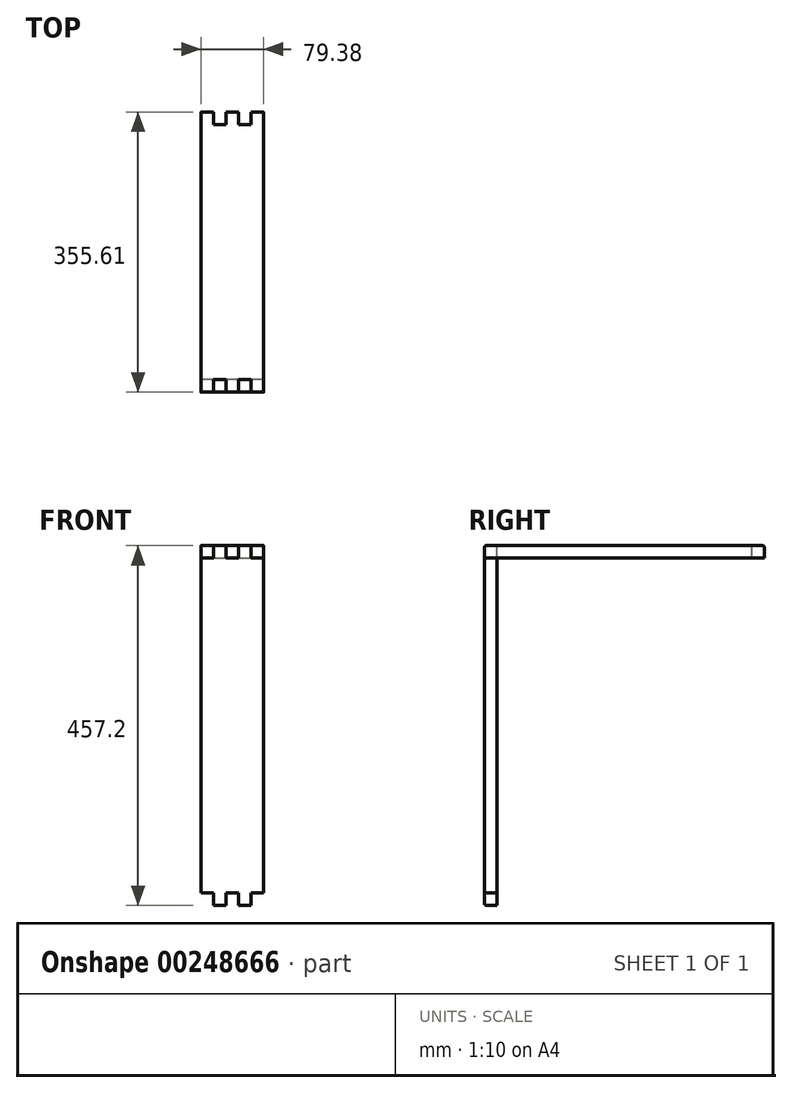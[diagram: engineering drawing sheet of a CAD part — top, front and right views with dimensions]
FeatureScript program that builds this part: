
annotation { "Feature Type Name" : "Feature", "Feature Type Description" : "" }
export const myFeature = defineFeature(function(context is Context, id is Id, definition is map)
    precondition{}
    {
        {
            var Q0;
            Q0=qCreatedBy(makeId("Front.planeOp"),FACE);
            var sketch = newSketch(context, id + "F0", { "sketchPlane" : qUnion([Q0])});
            skLineSegment(sketch, "E0.bottom", {"start": v(0, 0) * mm, "end": v(79.38, 0) * mm});
            skLineSegment(sketch, "E0.top", {"start": v(0, 457.2) * mm, "end": v(79.37, 457.2) * mm});
            skLineSegment(sketch, "E0.left", {"start": v(0, 0) * mm, "end": v(0, 457.2) * mm});
            skLineSegment(sketch, "E0.right", {"start": v(79.38, 0) * mm, "end": v(79.37, 457.2) * mm});
            skSolve(sketch);
        }
        {
            var Q0;
            Q0 = qSketchRegion(id + "F0", true);
            extrude(context, id + "F1", {"entities" : qUnion([Q0]), "depth" : 15.88 * mm});
        }
        {
            var Q0;
            Q0=makeQuery(id+"F1.opExtrude","CAP_FACE",FACE,{"disambiguationData":[OSD([sQuery(id+"F0.wireOp",EDGE,"E0.bottom"),sQuery(id+"F0.wireOp",EDGE,"E0.top"),sQuery(id+"F0.wireOp",EDGE,"E0.left"),sQuery(id+"F0.wireOp",EDGE,"E0.right")])],"isStart":false});
            var sketch = newSketch(context, id + "F2", { "sketchPlane" : qUnion([Q0])});
            skLineSegment(sketch, "E1.bottom", {"start": v(0, 457.2) * mm, "end": v(15.87, 457.2) * mm});
            skLineSegment(sketch, "E1.top", {"start": v(0, 441.33) * mm, "end": v(15.88, 441.33) * mm});
            skLineSegment(sketch, "E1.left", {"start": v(0, 457.2) * mm, "end": v(0, 441.33) * mm});
            skLineSegment(sketch, "E1.right", {"start": v(15.88, 457.2) * mm, "end": v(15.88, 441.33) * mm});
            skLineSegment(sketch, "E2.0.1.0", {"start": v(0, 15.88) * mm, "end": v(15.87, 15.88) * mm});
            skLineSegment(sketch, "E2.0.1.1", {"start": v(15.88, 15.88) * mm, "end": v(15.88, 0) * mm});
            skLineSegment(sketch, "E2.0.1.2", {"start": v(0, 0) * mm, "end": v(15.88, 0) * mm});
            skLineSegment(sketch, "E2.0.1.3", {"start": v(0, 15.88) * mm, "end": v(0, 0) * mm});
            skLineSegment(sketch, "E2.1.0.0", {"start": v(31.75, 457.2) * mm, "end": v(47.62, 457.2) * mm});
            skLineSegment(sketch, "E2.1.0.1", {"start": v(47.62, 457.2) * mm, "end": v(47.62, 441.33) * mm});
            skLineSegment(sketch, "E2.1.0.2", {"start": v(31.75, 441.33) * mm, "end": v(47.62, 441.33) * mm});
            skLineSegment(sketch, "E2.1.0.3", {"start": v(31.75, 457.2) * mm, "end": v(31.75, 441.33) * mm});
            skLineSegment(sketch, "E2.1.1.0", {"start": v(31.75, 15.88) * mm, "end": v(47.62, 15.88) * mm});
            skLineSegment(sketch, "E2.1.1.1", {"start": v(47.62, 15.88) * mm, "end": v(47.62, 0) * mm});
            skLineSegment(sketch, "E2.1.1.2", {"start": v(31.75, 0) * mm, "end": v(47.62, 0) * mm});
            skLineSegment(sketch, "E2.1.1.3", {"start": v(31.75, 15.88) * mm, "end": v(31.75, 0) * mm});
            skLineSegment(sketch, "E2.2.0.0", {"start": v(63.5, 457.2) * mm, "end": v(79.38, 457.2) * mm});
            skLineSegment(sketch, "E2.2.0.1", {"start": v(79.38, 457.2) * mm, "end": v(79.38, 441.33) * mm});
            skLineSegment(sketch, "E2.2.0.2", {"start": v(63.5, 441.33) * mm, "end": v(79.38, 441.33) * mm});
            skLineSegment(sketch, "E2.2.0.3", {"start": v(63.5, 457.2) * mm, "end": v(63.5, 441.33) * mm});
            skLineSegment(sketch, "E2.2.1.0", {"start": v(63.5, 15.88) * mm, "end": v(79.38, 15.88) * mm});
            skLineSegment(sketch, "E2.2.1.1", {"start": v(79.38, 15.88) * mm, "end": v(79.38, 0) * mm});
            skLineSegment(sketch, "E2.2.1.2", {"start": v(63.5, 0) * mm, "end": v(79.38, 0) * mm});
            skLineSegment(sketch, "E2.2.1.3", {"start": v(63.5, 15.88) * mm, "end": v(63.5, 0) * mm});
            skLineSegment(sketch, "E2.direction1", {"start": v(0, 457.2) * mm, "end": v(31.75, 457.2) * mm, "construction": true});
            skLineSegment(sketch, "E2.direction2", {"start": v(0, 457.2) * mm, "end": v(0, 15.88) * mm, "construction": true});
            skSolve(sketch);
        }
        {
            var Q0;
            Q0 = qSketchRegion(id + "F2", true);
            extrude(context, id + "F3", {"entities" : qUnion([Q0]), "operationType" : NewBodyOperationType.REMOVE, "endBound" : BoundingType.UP_TO_NEXT, "oppositeDirection" : true, "depth" : 25.4 * mm});
        }
        {
            var Q0;
            {var subQ2=sQuery(id+"F0.wireOp",EDGE,"E0.top");Q0=makeQuery(id+"F3.boolean.opBoolean","SPLIT",FACE,{"disambiguationData":[TD([makeQuery(id+"F3.opExtrude","SWEPT_FACE",FACE,{"disambiguationData":[OSD([sQuery(id+"F2.wireOp",EDGE,"E1.right")])]})])],"derivedFrom":makeQuery(id+"F1.opExtrude","SWEPT_FACE",FACE,{"disambiguationData":[OSD([subQ2])]})});}
            var sketch = newSketch(context, id + "F4", { "sketchPlane" : qUnion([Q0])});
            skLineSegment(sketch, "E3.0", {"start": v(0, 0) * mm, "end": v(0, -15.87) * mm, "construction": true});
            skLineSegment(sketch, "E3.1", {"start": v(0, -15.88) * mm, "end": v(15.88, -15.88) * mm, "construction": true});
            skLineSegment(sketch, "E4.bottom", {"start": v(0, -15.87) * mm, "end": v(79.37, -15.87) * mm});
            skLineSegment(sketch, "E4.top", {"start": v(0, 339.73) * mm, "end": v(79.37, 339.73) * mm});
            skLineSegment(sketch, "E4.left", {"start": v(0, -15.87) * mm, "end": v(0, 339.73) * mm});
            skLineSegment(sketch, "E4.right", {"start": v(79.37, -15.88) * mm, "end": v(79.37, 339.73) * mm});
            skLineSegment(sketch, "E5.0", {"start": v(79.37, 0) * mm, "end": v(79.37, -15.87) * mm, "construction": true});
            skSolve(sketch);
        }
        {
            var Q0;
            Q0 = qSketchRegion(id + "F4", true);
            extrude(context, id + "F5", {"entities" : qUnion([Q0]), "oppositeDirection" : true, "depth" : 15.88 * mm});
        }
        {
            var Q0;
            Q0=makeQuery(id+"F1.opExtrude","SWEPT_BODY",BODY,{"disambiguationData":[OSD([sQuery(id+"F0.wireOp",EDGE,"E0.bottom"),sQuery(id+"F0.wireOp",EDGE,"E0.top"),sQuery(id+"F0.wireOp",EDGE,"E0.left"),sQuery(id+"F0.wireOp",EDGE,"E0.right")])]});
            var Q1;
            Q1=makeQuery(id+"F5.opExtrude","SWEPT_BODY",BODY,{"disambiguationData":[OSD([sQuery(id+"F4.wireOp",EDGE,"E4.bottom"),sQuery(id+"F4.wireOp",EDGE,"E4.top"),sQuery(id+"F4.wireOp",EDGE,"E4.left"),sQuery(id+"F4.wireOp",EDGE,"E4.right")])]});
            booleanBodies(context, id + "F6", {"operationType" : BooleanOperationType.SUBTRACTION, "tools" : qUnion([Q0]), "targets" : qUnion([Q1]), "keepTools" : true});
        }
        {
            var Q0;
            {var subQ3=sQuery(id+"F4.wireOp",EDGE,"E4.bottom");Q0=makeQuery(id+"F6.opBoolean","SPLIT",FACE,{"disambiguationData":[TD([makeQuery(id+"F3.boolean.opBoolean","COPY",FACE,{"derivedFrom":makeQuery(id+"F3.opExtrude","SWEPT_FACE",FACE,{"disambiguationData":[OSD([sQuery(id+"F2.wireOp",EDGE,"E1.right")])]})})])],"derivedFrom":makeQuery(id+"F5.opExtrude","SWEPT_FACE",FACE,{"disambiguationData":[OSD([subQ3])]})});}
            var Q1;
            Q1=makeQuery(id+"F5.opExtrude","SWEPT_FACE",FACE,{"disambiguationData":[OSD([sQuery(id+"F4.wireOp",EDGE,"E4.top")])]});
            cPlane(context, id + "F7", {"entities" : qUnion([Q0, Q1]), "cplaneType" : CPlaneType.MID_PLANE, "offset" : 25.4 * mm, "width" : 152.4 * mm, "height" : 152.4 * mm});
        }
        {
            var Q0;
            Q0=makeQuery(id+"F5.opExtrude","CAP_FACE",FACE,{"disambiguationData":[OSD([sQuery(id+"F4.wireOp",EDGE,"E4.bottom"),sQuery(id+"F4.wireOp",EDGE,"E4.top"),sQuery(id+"F4.wireOp",EDGE,"E4.left"),sQuery(id+"F4.wireOp",EDGE,"E4.right")])],"isStart":true});
            var sketch = newSketch(context, id + "F8", { "sketchPlane" : qUnion([Q0])});
            skLineSegment(sketch, "E6.0.0", {"start": v(31.75, 0) * mm, "end": v(15.88, 0) * mm, "construction": true});
            skLineSegment(sketch, "E6.0.1", {"start": v(15.88, 0) * mm, "end": v(15.88, -15.87) * mm, "construction": true});
            skLineSegment(sketch, "E6.0.2", {"start": v(15.88, -15.88) * mm, "end": v(31.75, -15.88) * mm, "construction": true});
            skLineSegment(sketch, "E6.0.3", {"start": v(31.75, -15.87) * mm, "end": v(31.75, 0) * mm, "construction": true});
            skLineSegment(sketch, "E6.1.0", {"start": v(63.5, -15.87) * mm, "end": v(63.5, 0) * mm, "construction": true});
            skLineSegment(sketch, "E6.1.1", {"start": v(63.5, 0) * mm, "end": v(47.62, 0) * mm, "construction": true});
            skLineSegment(sketch, "E6.1.2", {"start": v(47.62, 0) * mm, "end": v(47.62, -15.87) * mm, "construction": true});
            skLineSegment(sketch, "E6.1.3", {"start": v(47.62, -15.88) * mm, "end": v(63.5, -15.88) * mm, "construction": true});
            skLineSegment(sketch, "E7.MirrorCS", {"start": v(31.75, 339.72) * mm, "end": v(31.75, 323.85) * mm});
            skLineSegment(sketch, "E8.MirrorCS", {"start": v(63.5, 339.72) * mm, "end": v(63.5, 323.85) * mm});
            skLineSegment(sketch, "E9.MirrorCS", {"start": v(63.5, 323.85) * mm, "end": v(47.62, 323.85) * mm});
            skLineSegment(sketch, "E10.MirrorCS", {"start": v(47.62, 323.85) * mm, "end": v(47.62, 339.72) * mm});
            skLineSegment(sketch, "E11.MirrorCS", {"start": v(47.62, 339.73) * mm, "end": v(63.5, 339.73) * mm});
            skLineSegment(sketch, "E12.MirrorCS", {"start": v(15.88, 339.73) * mm, "end": v(31.75, 339.73) * mm});
            skLineSegment(sketch, "E13.MirrorCS", {"start": v(15.88, 323.85) * mm, "end": v(15.88, 339.72) * mm});
            skLineSegment(sketch, "E14.MirrorCS", {"start": v(31.75, 323.85) * mm, "end": v(15.88, 323.85) * mm});
            skSolve(sketch);
        }
        {
            var Q0;
            Q0=makeQuery(id+"F8.imprint","IMPRINT",FACE,{"disambiguationData":[TD([[makeQuery(id+"F8.imprint","IMPRINT",EDGE,{"derivedFrom":sQuery(id+"F8.wireOp",EDGE,"E7.MirrorCS")}),-1.0]])]});
            var Q1;
            Q1=makeQuery(id+"F8.imprint","IMPRINT",FACE,{"disambiguationData":[TD([[makeQuery(id+"F8.imprint","IMPRINT",EDGE,{"derivedFrom":sQuery(id+"F8.wireOp",EDGE,"E8.MirrorCS")}),-1.0]])]});
            var Q2;
            Q2 = qConstructionFilter(qBodyType(qCreatedBy(id + "F8" ,EDGE), BodyType.WIRE), ConstructionObject.NO);
            extrude(context, id + "F9", {"entities" : qUnion([Q0, Q1]), "operationType" : NewBodyOperationType.REMOVE, "surfaceEntities" : qUnion([Q2]), "endBound" : BoundingType.UP_TO_NEXT, "oppositeDirection" : true, "depth" : 25.4 * mm});
        }
        {
            var Q0;
            {var subQ0=sQuery(id+"F4.wireOp",EDGE,"E4.bottom");Q0=makeQuery(id+"F6.opBoolean","SPLIT",EDGE,{"disambiguationData":[TD([makeQuery(id+"F3.boolean.opBoolean","COPY",FACE,{"derivedFrom":makeQuery(id+"F3.opExtrude","SWEPT_FACE",FACE,{"disambiguationData":[OSD([sQuery(id+"F2.wireOp",EDGE,"E2.2.0.3")])]})})])],"derivedFrom":makeQuery(id+"F5.opExtrude","CAP_EDGE",EDGE,{"disambiguationData":[OSD([subQ0])],"isStart":true})});}
            var Q1;
            {var subQ0=sQuery(id+"F0.wireOp",EDGE,"E0.top");Q1=makeQuery(id+"F3.boolean.opBoolean","SPLIT",EDGE,{"disambiguationData":[TD([makeQuery(id+"F3.opExtrude","SWEPT_FACE",FACE,{"disambiguationData":[OSD([sQuery(id+"F2.wireOp",EDGE,"E2.1.0.1")])]})])],"derivedFrom":makeQuery(id+"F1.opExtrude","CAP_EDGE",EDGE,{"disambiguationData":[OSD([subQ0])],"isStart":false})});}
            var Q2;
            {var subQ0=sQuery(id+"F4.wireOp",EDGE,"E4.bottom");Q2=makeQuery(id+"F6.opBoolean","SPLIT",EDGE,{"disambiguationData":[TD([makeQuery(id+"F3.boolean.opBoolean","COPY",FACE,{"derivedFrom":makeQuery(id+"F3.opExtrude","SWEPT_FACE",FACE,{"disambiguationData":[OSD([sQuery(id+"F2.wireOp",EDGE,"E2.1.0.1")])]})})])],"derivedFrom":makeQuery(id+"F5.opExtrude","CAP_EDGE",EDGE,{"disambiguationData":[OSD([subQ0])],"isStart":true})});}
            var Q3;
            {var subQ0=sQuery(id+"F0.wireOp",EDGE,"E0.top");Q3=makeQuery(id+"F3.boolean.opBoolean","SPLIT",EDGE,{"disambiguationData":[TD([makeQuery(id+"F3.opExtrude","SWEPT_FACE",FACE,{"disambiguationData":[OSD([sQuery(id+"F2.wireOp",EDGE,"E1.right")])]})])],"derivedFrom":makeQuery(id+"F1.opExtrude","CAP_EDGE",EDGE,{"disambiguationData":[OSD([subQ0])],"isStart":false})});}
            var Q4;
            {var subQ0=sQuery(id+"F4.wireOp",EDGE,"E4.bottom");Q4=makeQuery(id+"F6.opBoolean","SPLIT",EDGE,{"disambiguationData":[TD([makeQuery(id+"F3.boolean.opBoolean","COPY",FACE,{"derivedFrom":makeQuery(id+"F3.opExtrude","SWEPT_FACE",FACE,{"disambiguationData":[OSD([sQuery(id+"F2.wireOp",EDGE,"E1.right")])]})})])],"derivedFrom":makeQuery(id+"F5.opExtrude","CAP_EDGE",EDGE,{"disambiguationData":[OSD([subQ0])],"isStart":true})});}
            var Q5;
            {var subQ0=sQuery(id+"F4.wireOp",EDGE,"E4.right");var subQ1=sQuery(id+"F4.wireOp",EDGE,"E4.top");Q5=makeQuery(id+"F9.boolean.opBoolean","SPLIT",EDGE,{"disambiguationData":[TD([makeQuery(id+"F5.opExtrude","SWEPT_FACE",FACE,{"disambiguationData":[OSD([subQ0])]})])],"derivedFrom":makeQuery(id+"F5.opExtrude","CAP_EDGE",EDGE,{"disambiguationData":[OSD([subQ1])],"isStart":true})});}
            var Q6;
            {var subQ0=sQuery(id+"F4.wireOp",EDGE,"E4.top");Q6=makeQuery(id+"F9.boolean.opBoolean","SPLIT",EDGE,{"disambiguationData":[TD([makeQuery(id+"F9.opExtrude","SWEPT_FACE",FACE,{"disambiguationData":[OSD([sQuery(id+"F8.wireOp",EDGE,"E7.MirrorCS")])]})])],"derivedFrom":makeQuery(id+"F5.opExtrude","CAP_EDGE",EDGE,{"disambiguationData":[OSD([subQ0])],"isStart":true})});}
            var Q7;
            {var subQ0=sQuery(id+"F4.wireOp",EDGE,"E4.left");var subQ1=sQuery(id+"F4.wireOp",EDGE,"E4.top");Q7=makeQuery(id+"F9.boolean.opBoolean","SPLIT",EDGE,{"disambiguationData":[TD([makeQuery(id+"F5.opExtrude","SWEPT_FACE",FACE,{"disambiguationData":[OSD([subQ0])]})])],"derivedFrom":makeQuery(id+"F5.opExtrude","CAP_EDGE",EDGE,{"disambiguationData":[OSD([subQ1])],"isStart":true})});}
            var Q8;
            {var subQ0=sQuery(id+"F0.wireOp",EDGE,"E0.bottom");Q8=makeQuery(id+"F3.boolean.opBoolean","SPLIT",EDGE,{"disambiguationData":[TD([makeQuery(id+"F3.opExtrude","SWEPT_FACE",FACE,{"disambiguationData":[OSD([sQuery(id+"F2.wireOp",EDGE,"E2.0.1.1")])]})])],"derivedFrom":makeQuery(id+"F1.opExtrude","CAP_EDGE",EDGE,{"disambiguationData":[OSD([subQ0])],"isStart":false})});}
            var Q9;
            {var subQ0=sQuery(id+"F0.wireOp",EDGE,"E0.bottom");Q9=makeQuery(id+"F3.boolean.opBoolean","SPLIT",EDGE,{"disambiguationData":[TD([makeQuery(id+"F3.opExtrude","SWEPT_FACE",FACE,{"disambiguationData":[OSD([sQuery(id+"F2.wireOp",EDGE,"E2.1.1.1")])]})])],"derivedFrom":makeQuery(id+"F1.opExtrude","CAP_EDGE",EDGE,{"disambiguationData":[OSD([subQ0])],"isStart":false})});}
            fillet(context, id + "F10", {"entities" : qUnion([Q0, Q1, Q2, Q3, Q4, Q5, Q6, Q7, Q8, Q9]), "radius" : 2.54 * mm, "tangentPropagation" : true, "allowEdgeOverflow" : false});
        }
    });
